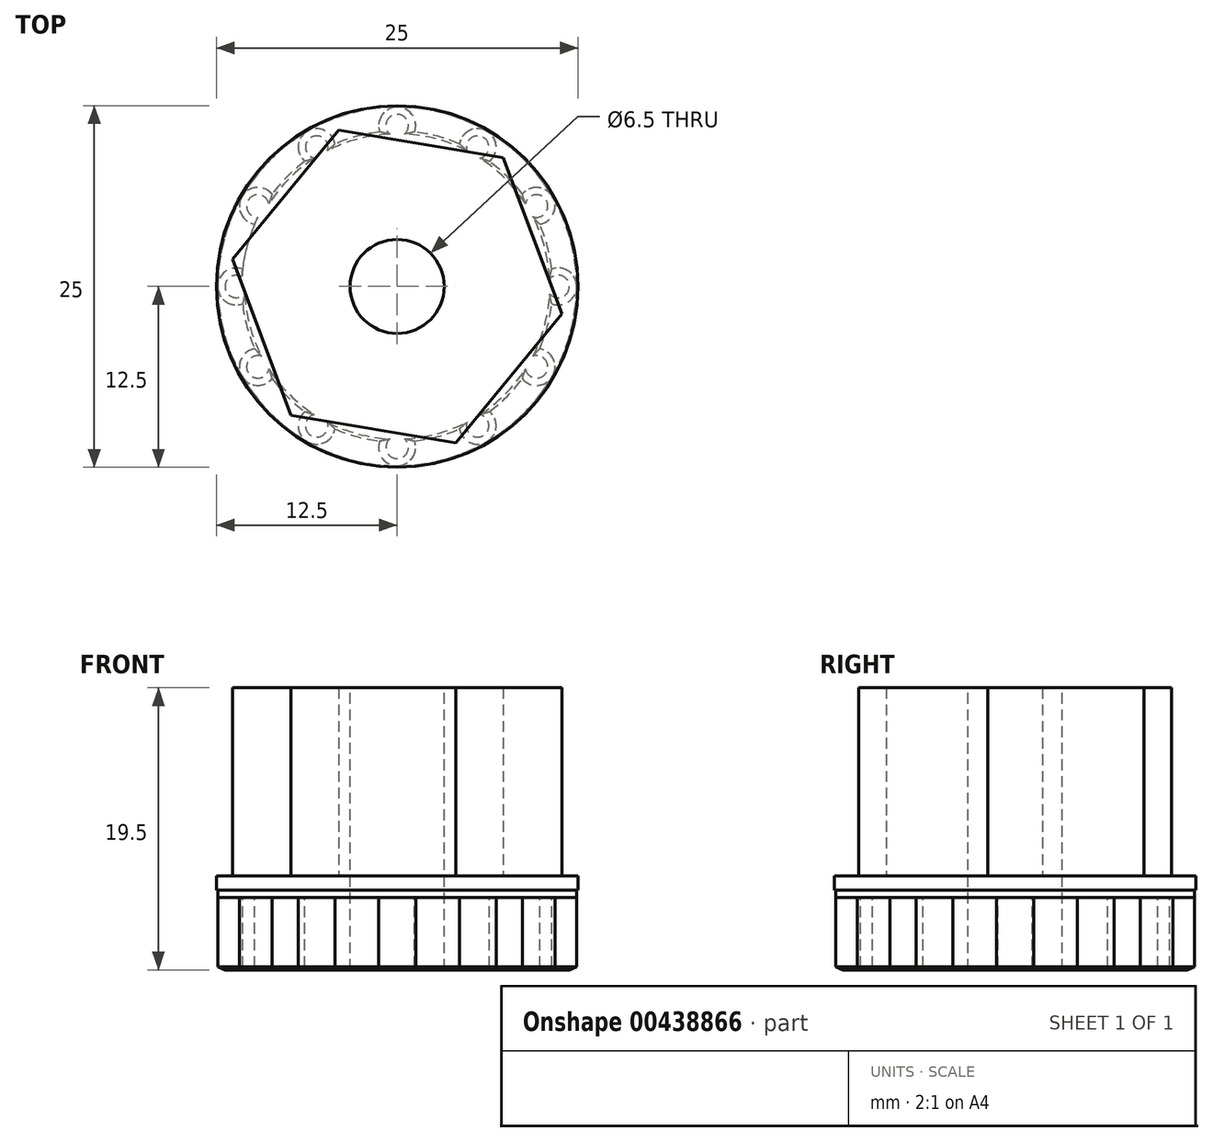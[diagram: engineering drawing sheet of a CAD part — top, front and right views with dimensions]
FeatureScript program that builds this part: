
annotation { "Feature Type Name" : "Feature", "Feature Type Description" : "" }
export const myFeature = defineFeature(function(context is Context, id is Id, definition is map)
    precondition{}
    {
        {
            var Q0;
            Q0=qCreatedBy(makeId("Top.planeOp"),FACE);
            var sketch = newSketch(context, id + "F0", { "sketchPlane" : qUnion([Q0])});
            skCircle(sketch, "E0", {"center": v(0, 0) * mm, "radius": 12.5 * mm});
            skSolve(sketch);
        }
        {
            var Q0;
            Q0 = qSketchRegion(id + "F0", true);
            extrude(context, id + "F1", {"entities" : qUnion([Q0]), "depth" : 1 * mm});
        }
        {
            var Q0;
            Q0=makeQuery(id+"F1.opExtrude","CAP_FACE",FACE,{"disambiguationData":[OSD([sQuery(id+"F0.wireOp",EDGE,"E0")])],"isStart":false});
            var sketch = newSketch(context, id + "F2", { "sketchPlane" : qUnion([Q0])});
            skCircle(sketch, "E1.cCircle", {"center": v(0, 0) * mm, "radius": 10 * mm, "construction": true});
            skLineSegment(sketch, "E1.0", {"start": v(7.34, 8.92) * mm, "end": v(11.4, -1.9) * mm});
            skLineSegment(sketch, "E1.1", {"start": v(11.4, -1.9) * mm, "end": v(4.05, -10.81) * mm});
            skLineSegment(sketch, "E1.2", {"start": v(4.05, -10.81) * mm, "end": v(-7.34, -8.92) * mm});
            skLineSegment(sketch, "E1.3", {"start": v(-7.34, -8.92) * mm, "end": v(-11.4, 1.9) * mm});
            skLineSegment(sketch, "E1.4", {"start": v(-11.4, 1.9) * mm, "end": v(-4.05, 10.81) * mm});
            skLineSegment(sketch, "E1.5", {"start": v(-4.05, 10.81) * mm, "end": v(7.34, 8.92) * mm});
            skPoint(sketch, "E1.0.midPoint", {"position": v(9.36, 3.51) * mm});
            skSolve(sketch);
        }
        {
            var Q0;
            Q0 = qSketchRegion(id + "F2", true);
            extrude(context, id + "F3", {"entities" : qUnion([Q0]), "operationType" : NewBodyOperationType.ADD, "depth" : 13 * mm});
        }
        {
            var Q0;
            Q0=makeQuery(id+"F1.opExtrude","CAP_FACE",FACE,{"disambiguationData":[OSD([sQuery(id+"F0.wireOp",EDGE,"E0")])],"isStart":true});
            var sketch = newSketch(context, id + "F4", { "sketchPlane" : qUnion([Q0])});
            skCircle(sketch, "E2", {"center": v(0, 0) * mm, "radius": 12.4 * mm});
            skSolve(sketch);
        }
        {
            var Q0;
            Q0 = qSketchRegion(id + "F4", true);
            extrude(context, id + "F5", {"entities" : qUnion([Q0]), "operationType" : NewBodyOperationType.ADD, "depth" : 0.5 * mm});
        }
        {
            var Q0;
            Q0=makeQuery(id+"F5.opExtrude","CAP_FACE",FACE,{"disambiguationData":[OSD([sQuery(id+"F4.wireOp",EDGE,"E2")])],"isStart":false});
            var sketch = newSketch(context, id + "F6", { "sketchPlane" : qUnion([Q0])});
            skCircle(sketch, "E3", {"center": v(0, 0) * mm, "radius": 10.75 * mm});
            skLineSegment(sketch, "E4", {"start": v(0, 0) * mm, "end": v(0, 12.4) * mm, "construction": true});
            skArc(sketch, "E5", {"start": v(1.2, 10.68) * mm, "mid": v(0, 12.4) * mm, "end": v(-1.2, 10.68) * mm});
            skArc(sketch, "E6.1.0", {"start": v(-4.3, 9.85) * mm, "mid": v(-6.2, 10.74) * mm, "end": v(-6.38, 8.65) * mm});
            skArc(sketch, "E6.2.0", {"start": v(-8.65, 6.38) * mm, "mid": v(-10.74, 6.2) * mm, "end": v(-9.85, 4.3) * mm});
            skArc(sketch, "E6.3.0", {"start": v(-10.68, 1.2) * mm, "mid": v(-12.4, 0) * mm, "end": v(-10.68, -1.2) * mm});
            skArc(sketch, "E6.4.0", {"start": v(-9.85, -4.3) * mm, "mid": v(-10.74, -6.2) * mm, "end": v(-8.65, -6.38) * mm});
            skArc(sketch, "E6.5.0", {"start": v(-6.38, -8.65) * mm, "mid": v(-6.2, -10.74) * mm, "end": v(-4.3, -9.85) * mm});
            skArc(sketch, "E6.6.0", {"start": v(-1.2, -10.68) * mm, "mid": v(0, -12.4) * mm, "end": v(1.2, -10.68) * mm});
            skArc(sketch, "E6.7.0", {"start": v(4.3, -9.85) * mm, "mid": v(6.2, -10.74) * mm, "end": v(6.38, -8.65) * mm});
            skArc(sketch, "E6.8.0", {"start": v(8.65, -6.38) * mm, "mid": v(10.74, -6.2) * mm, "end": v(9.85, -4.3) * mm});
            skArc(sketch, "E6.9.0", {"start": v(10.68, -1.2) * mm, "mid": v(12.4, 0) * mm, "end": v(10.68, 1.2) * mm});
            skArc(sketch, "E6.10.0", {"start": v(9.85, 4.3) * mm, "mid": v(10.74, 6.2) * mm, "end": v(8.65, 6.38) * mm});
            skArc(sketch, "E7.3.11.0", {"start": v(6.38, 8.65) * mm, "mid": v(6.2, 10.74) * mm, "end": v(4.3, 9.85) * mm});
            skSolve(sketch);
        }
        {
            var Q0;
            Q0 = qSketchRegion(id + "F6", true);
            extrude(context, id + "F7", {"entities" : qUnion([Q0]), "operationType" : NewBodyOperationType.ADD, "depth" : 5 * mm});
        }
        {
            var Q0;
            Q0=makeQuery(id+"F3.opExtrude","CAP_FACE",FACE,{"disambiguationData":[OSD([sQuery(id+"F2.wireOp",EDGE,"E1.0"),sQuery(id+"F2.wireOp",EDGE,"E1.1"),sQuery(id+"F2.wireOp",EDGE,"E1.2"),sQuery(id+"F2.wireOp",EDGE,"E1.3"),sQuery(id+"F2.wireOp",EDGE,"E1.4"),sQuery(id+"F2.wireOp",EDGE,"E1.5")])],"isStart":false});
            var sketch = newSketch(context, id + "F8", { "sketchPlane" : qUnion([Q0])});
            skCircle(sketch, "E8", {"center": v(0, 0) * mm, "radius": 3.25 * mm});
            skSolve(sketch);
        }
        {
            var Q0;
            Q0 = qSketchRegion(id + "F8", true);
            extrude(context, id + "F9", {"entities" : qUnion([Q0]), "operationType" : NewBodyOperationType.REMOVE, "endBound" : BoundingType.THROUGH_ALL, "oppositeDirection" : true, "depth" : 25 * mm});
        }
        {
            var Q0;
            Q0=makeQuery(id+"F7.opExtrude","CAP_EDGE",EDGE,{"disambiguationData":[OSD([sQuery(id+"F6.wireOp",EDGE,"E6.5.0")])],"isStart":false});
            var Q1;
            Q1=makeQuery(id+"F7.opExtrude","CAP_EDGE",EDGE,{"disambiguationData":[OSD([sQuery(id+"F6.wireOp",EDGE,"E6.6.0")])],"isStart":false});
            var Q2;
            Q2=makeQuery(id+"F7.opExtrude","CAP_EDGE",EDGE,{"disambiguationData":[OSD([sQuery(id+"F6.wireOp",EDGE,"E6.7.0")])],"isStart":false});
            var Q3;
            Q3=makeQuery(id+"F7.opExtrude","CAP_EDGE",EDGE,{"disambiguationData":[OSD([sQuery(id+"F6.wireOp",EDGE,"E6.8.0")])],"isStart":false});
            var Q4;
            Q4=makeQuery(id+"F7.opExtrude","CAP_EDGE",EDGE,{"disambiguationData":[OSD([sQuery(id+"F6.wireOp",EDGE,"E6.9.0")])],"isStart":false});
            var Q5;
            Q5=makeQuery(id+"F7.opExtrude","CAP_EDGE",EDGE,{"disambiguationData":[OSD([sQuery(id+"F6.wireOp",EDGE,"E6.10.0")])],"isStart":false});
            var Q6;
            Q6=makeQuery(id+"F7.opExtrude","CAP_EDGE",EDGE,{"disambiguationData":[OSD([sQuery(id+"F6.wireOp",EDGE,"E7.3.11.0")])],"isStart":false});
            var Q7;
            Q7=makeQuery(id+"F7.opExtrude","CAP_EDGE",EDGE,{"disambiguationData":[OSD([sQuery(id+"F6.wireOp",EDGE,"E5")])],"isStart":false});
            var Q8;
            Q8=makeQuery(id+"F7.opExtrude","CAP_EDGE",EDGE,{"disambiguationData":[OSD([sQuery(id+"F6.wireOp",EDGE,"E6.1.0")])],"isStart":false});
            var Q9;
            Q9=makeQuery(id+"F7.opExtrude","CAP_EDGE",EDGE,{"disambiguationData":[OSD([sQuery(id+"F6.wireOp",EDGE,"E6.2.0")])],"isStart":false});
            var Q10;
            Q10=makeQuery(id+"F7.opExtrude","CAP_EDGE",EDGE,{"disambiguationData":[OSD([sQuery(id+"F6.wireOp",EDGE,"E6.3.0")])],"isStart":false});
            var Q11;
            Q11=makeQuery(id+"F7.opExtrude","CAP_EDGE",EDGE,{"disambiguationData":[OSD([sQuery(id+"F6.wireOp",EDGE,"E6.4.0")])],"isStart":false});
            chamfer(context, id + "F10", {"entities" : qUnion([Q0, Q1, Q2, Q3, Q4, Q5, Q6, Q7, Q8, Q9, Q10, Q11]), "chamferType" : ChamferType.TWO_OFFSETS, "width1" : 0.5 * mm, "oppositeDirection" : false, "width2" : 0.2 * mm, "tangentPropagation" : true});
        }
        {
            var Q0;
            {var subQ0=sQuery(id+"F6.wireOp",EDGE,"E3");Q0=makeQuery(id+"F7.opExtrude","CAP_EDGE",EDGE,{"disambiguationData":[OSD([subQ0]),TDD([makeQuery(id+"F6.imprint","IMPRINT",EDGE,{"disambiguationData":[TD([[makeQuery(id+"F6.imprint","INTERSECT",VERTEX,{"disambiguationData":[OD(1.0)],"derivedFrom":[subQ0,sQuery(id+"F6.wireOp",EDGE,"E6.2.0")]}),-1.0]])],"derivedFrom":subQ0})])],"isStart":false});}
            var Q1;
            {var subQ0=sQuery(id+"F6.wireOp",EDGE,"E3");Q1=makeQuery(id+"F7.opExtrude","CAP_EDGE",EDGE,{"disambiguationData":[OSD([subQ0]),TDD([makeQuery(id+"F6.imprint","IMPRINT",EDGE,{"disambiguationData":[TD([[makeQuery(id+"F6.imprint","INTERSECT",VERTEX,{"disambiguationData":[OD(1.0)],"derivedFrom":[subQ0,sQuery(id+"F6.wireOp",EDGE,"E6.1.0")]}),-1.0]])],"derivedFrom":subQ0})])],"isStart":false});}
            var Q2;
            {var subQ0=sQuery(id+"F6.wireOp",EDGE,"E3");Q2=makeQuery(id+"F7.opExtrude","CAP_EDGE",EDGE,{"disambiguationData":[OSD([subQ0]),TDD([makeQuery(id+"F6.imprint","IMPRINT",EDGE,{"disambiguationData":[TD([[makeQuery(id+"F6.imprint","INTERSECT",VERTEX,{"disambiguationData":[OD(1.0)],"derivedFrom":[subQ0,sQuery(id+"F6.wireOp",EDGE,"E5")]}),-1.0]])],"derivedFrom":subQ0})])],"isStart":false});}
            var Q3;
            {var subQ0=sQuery(id+"F6.wireOp",EDGE,"E3");Q3=makeQuery(id+"F7.opExtrude","CAP_EDGE",EDGE,{"disambiguationData":[OSD([subQ0]),TDD([makeQuery(id+"F6.imprint","IMPRINT",EDGE,{"disambiguationData":[TD([[makeQuery(id+"F6.imprint","INTERSECT",VERTEX,{"disambiguationData":[OD(0.0)],"derivedFrom":[subQ0,sQuery(id+"F6.wireOp",EDGE,"E5")]}),1.0]])],"derivedFrom":subQ0})])],"isStart":false});}
            var Q4;
            {var subQ0=sQuery(id+"F6.wireOp",EDGE,"E3");Q4=makeQuery(id+"F7.opExtrude","CAP_EDGE",EDGE,{"disambiguationData":[OSD([subQ0]),TDD([makeQuery(id+"F6.imprint","IMPRINT",EDGE,{"disambiguationData":[TD([[makeQuery(id+"F6.imprint","INTERSECT",VERTEX,{"disambiguationData":[OD(1.0)],"derivedFrom":[subQ0,sQuery(id+"F6.wireOp",EDGE,"E6.10.0")]}),-1.0]])],"derivedFrom":subQ0})])],"isStart":false});}
            var Q5;
            {var subQ0=sQuery(id+"F6.wireOp",EDGE,"E3");Q5=makeQuery(id+"F7.opExtrude","CAP_EDGE",EDGE,{"disambiguationData":[OSD([subQ0]),TDD([makeQuery(id+"F6.imprint","IMPRINT",EDGE,{"disambiguationData":[TD([[makeQuery(id+"F6.imprint","INTERSECT",VERTEX,{"disambiguationData":[OD(1.0)],"derivedFrom":[subQ0,sQuery(id+"F6.wireOp",EDGE,"E6.9.0")]}),-1.0]])],"derivedFrom":subQ0})])],"isStart":false});}
            var Q6;
            {var subQ0=sQuery(id+"F6.wireOp",EDGE,"E3");Q6=makeQuery(id+"F7.opExtrude","CAP_EDGE",EDGE,{"disambiguationData":[OSD([subQ0]),TDD([makeQuery(id+"F6.imprint","IMPRINT",EDGE,{"disambiguationData":[TD([[makeQuery(id+"F6.imprint","INTERSECT",VERTEX,{"disambiguationData":[OD(1.0)],"derivedFrom":[subQ0,sQuery(id+"F6.wireOp",EDGE,"E6.8.0")]}),-1.0]])],"derivedFrom":subQ0})])],"isStart":false});}
            var Q7;
            {var subQ0=sQuery(id+"F6.wireOp",EDGE,"E3");Q7=makeQuery(id+"F7.opExtrude","CAP_EDGE",EDGE,{"disambiguationData":[OSD([subQ0]),TDD([makeQuery(id+"F6.imprint","IMPRINT",EDGE,{"disambiguationData":[TD([[makeQuery(id+"F6.imprint","INTERSECT",VERTEX,{"disambiguationData":[OD(1.0)],"derivedFrom":[subQ0,sQuery(id+"F6.wireOp",EDGE,"E6.7.0")]}),-1.0]])],"derivedFrom":subQ0})])],"isStart":false});}
            var Q8;
            {var subQ0=sQuery(id+"F6.wireOp",EDGE,"E3");Q8=makeQuery(id+"F7.opExtrude","CAP_EDGE",EDGE,{"disambiguationData":[OSD([subQ0]),TDD([makeQuery(id+"F6.imprint","IMPRINT",EDGE,{"disambiguationData":[TD([[makeQuery(id+"F6.imprint","INTERSECT",VERTEX,{"disambiguationData":[OD(1.0)],"derivedFrom":[subQ0,sQuery(id+"F6.wireOp",EDGE,"E6.6.0")]}),-1.0]])],"derivedFrom":subQ0})])],"isStart":false});}
            var Q9;
            {var subQ0=sQuery(id+"F6.wireOp",EDGE,"E3");Q9=makeQuery(id+"F7.opExtrude","CAP_EDGE",EDGE,{"disambiguationData":[OSD([subQ0]),TDD([makeQuery(id+"F6.imprint","IMPRINT",EDGE,{"disambiguationData":[TD([[makeQuery(id+"F6.imprint","INTERSECT",VERTEX,{"disambiguationData":[OD(1.0)],"derivedFrom":[subQ0,sQuery(id+"F6.wireOp",EDGE,"E6.5.0")]}),-1.0]])],"derivedFrom":subQ0})])],"isStart":false});}
            var Q10;
            {var subQ0=sQuery(id+"F6.wireOp",EDGE,"E3");Q10=makeQuery(id+"F7.opExtrude","CAP_EDGE",EDGE,{"disambiguationData":[OSD([subQ0]),TDD([makeQuery(id+"F6.imprint","IMPRINT",EDGE,{"disambiguationData":[TD([[makeQuery(id+"F6.imprint","INTERSECT",VERTEX,{"disambiguationData":[OD(1.0)],"derivedFrom":[subQ0,sQuery(id+"F6.wireOp",EDGE,"E6.4.0")]}),-1.0]])],"derivedFrom":subQ0})])],"isStart":false});}
            var Q11;
            {var subQ0=sQuery(id+"F6.wireOp",EDGE,"E3");Q11=makeQuery(id+"F7.opExtrude","CAP_EDGE",EDGE,{"disambiguationData":[OSD([subQ0]),TDD([makeQuery(id+"F6.imprint","IMPRINT",EDGE,{"disambiguationData":[TD([[makeQuery(id+"F6.imprint","INTERSECT",VERTEX,{"disambiguationData":[OD(1.0)],"derivedFrom":[subQ0,sQuery(id+"F6.wireOp",EDGE,"E6.3.0")]}),-1.0]])],"derivedFrom":subQ0})])],"isStart":false});}
            chamfer(context, id + "F11", {"entities" : qUnion([Q0, Q1, Q2, Q3, Q4, Q5, Q6, Q7, Q8, Q9, Q10, Q11]), "width" : 0.2 * mm, "tangentPropagation" : true});
        }
    });
